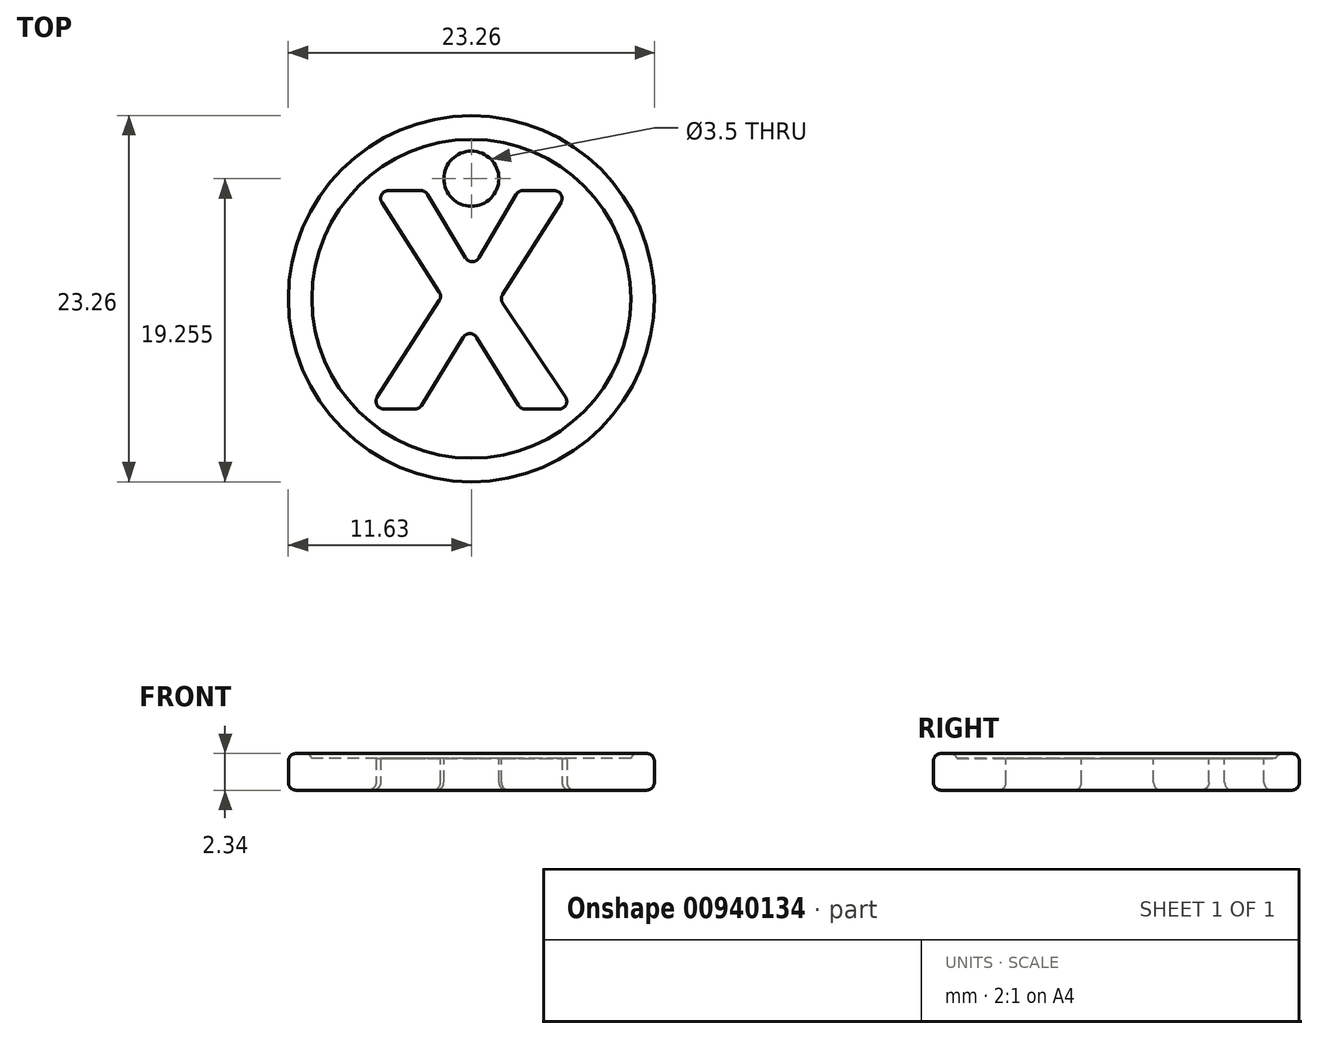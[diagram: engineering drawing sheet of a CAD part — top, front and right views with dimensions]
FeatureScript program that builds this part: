
annotation { "Feature Type Name" : "Feature", "Feature Type Description" : "" }
export const myFeature = defineFeature(function(context is Context, id is Id, definition is map)
    precondition{}
    {
        {
            var Q0;
            Q0=qCreatedBy(makeId("Front.planeOp"),FACE);
            var sketch = newSketch(context, id + "F0", { "sketchPlane" : qUnion([Q0])});
            skLineSegment(sketch, "E0", {"start": v(0, 0.86) * mm, "end": v(10.12, 0.86) * mm});
            skLineSegment(sketch, "E1", {"start": v(10.13, 0.86) * mm, "end": v(10.13, 1.17) * mm});
            skLineSegment(sketch, "E2", {"start": v(10.13, 1.16) * mm, "end": v(11.63, 1.16) * mm});
            skLineSegment(sketch, "E3", {"start": v(11.63, 1.17) * mm, "end": v(11.63, -1.17) * mm});
            skLineSegment(sketch, "E4", {"start": v(11.63, -1.17) * mm, "end": v(10.13, -1.17) * mm});
            skLineSegment(sketch, "E5", {"start": v(10.13, -1.17) * mm, "end": v(10.13, -1.16) * mm});
            skLineSegment(sketch, "E6", {"start": v(10.12, -1.17) * mm, "end": v(0, -1.17) * mm});
            skLineSegment(sketch, "E7", {"start": v(0, -1.17) * mm, "end": v(0, 0.86) * mm});
            skLineSegment(sketch, "E8", {"start": v(0, 10.48) * mm, "end": v(0, -13.78) * mm, "construction": true});
            skSolve(sketch);
        }
        {
            var Q0;
            Q0=makeQuery(id+"F0.imprint","IMPRINT",FACE,{"disambiguationData":[TD([[makeQuery(id+"F0.imprint","IMPRINT",EDGE,{"derivedFrom":sQuery(id+"F0.wireOp",EDGE,"E0")}),-1.0]])]});
            var Q1;
            Q1=sQuery(id+"F0.wireOp",EDGE,"E8");
            revolve(context, id + "F1", {"surfaceOperationType" : NewSurfaceOperationType.NEW, "entities" : qUnion([Q0]), "axis" : qUnion([Q1]), "revolveType" : RevolveType.FULL});
        }
        {
            var Q0;
            Q0=makeQuery(id+"F1.opRevolve","SWEPT_FACE",FACE,{"disambiguationData":[OSD([sQuery(id+"F0.wireOp",EDGE,"E0")])]});
            var sketch = newSketch(context, id + "F2", { "sketchPlane" : qUnion([Q0])});
            skText(sketch, "E9", { "text": "X", "fontName": "NotoSans-Bold.ttf"});
            const initialGuessF2  = {"E9": [-0.00647, -0.00701, 1, 0, 0.014]};
            skSetInitialGuess(sketch, initialGuessF2);
            skSolve(sketch);
        }
        {
            var Q0;
            Q0 = qSketchRegion(id + "F2", true);
            extrude(context, id + "F3", {"entities" : qUnion([Q0]), "operationType" : NewBodyOperationType.REMOVE, "oppositeDirection" : true, "depth" : 25 * mm, "offsetDistance" : 25 * mm});
        }
        {
            var Q0;
            Q0=makeQuery(id+"F1.opRevolve","SWEPT_FACE",FACE,{"disambiguationData":[OSD([sQuery(id+"F0.wireOp",EDGE,"E0")])]});
            var sketch = newSketch(context, id + "F4", { "sketchPlane" : qUnion([Q0])});
            skPoint(sketch, "E10", {"position": v(0, 7.63) * mm});
            skSolve(sketch);
        }
        {
            var Q0;
            Q0=sQuery(id+"F4.wireOp",VERTEX,"E10");
            var Q1;
            Q1=makeQuery(id+"F1.opRevolve","SWEPT_BODY",BODY,{"disambiguationData":[OSD([sQuery(id+"F0.wireOp",EDGE,"E0"),sQuery(id+"F0.wireOp",EDGE,"E1"),sQuery(id+"F0.wireOp",EDGE,"E2"),sQuery(id+"F0.wireOp",EDGE,"E3"),sQuery(id+"F0.wireOp",EDGE,"E4"),sQuery(id+"F0.wireOp",EDGE,"E5"),sQuery(id+"F0.wireOp",EDGE,"E6"),sQuery(id+"F0.wireOp",EDGE,"E7")])]});
            hole(context, id + "F5", {"style" : HoleStyle.SIMPLE, "endStyle" : HoleEndStyle.THROUGH, "holeDiameter" : 3.5 * mm, "majorDiameter" : 5 * mm, "isTappedThrough" : true, "tappedDepth" : 12 * mm, "tapClearance" : 3, "locations" : qUnion([Q0]), "scope" : qUnion([Q1])});
        }
        {
            var Q0;
            Q0=makeQuery(id+"F1.opRevolve","SWEPT_EDGE",EDGE,{"disambiguationData":[OSD([sQuery(id+"F0.wireOp",EDGE,"E2"),sQuery(id+"F0.wireOp",EDGE,"E3")])]});
            var Q1;
            Q1=makeQuery(id+"F1.opRevolve","SWEPT_EDGE",EDGE,{"disambiguationData":[OSD([sQuery(id+"F0.wireOp",EDGE,"E1"),sQuery(id+"F0.wireOp",EDGE,"E2")])]});
            var Q2;
            Q2=makeQuery(id+"F1.opRevolve","SWEPT_FACE",FACE,{"disambiguationData":[OSD([sQuery(id+"F0.wireOp",EDGE,"E3")])]});
            fillet(context, id + "F6", {"entities" : qUnion([Q0, Q1, Q2]), "radius" : 0.5 * mm, "tangentPropagation" : true, "allowEdgeOverflow" : false});
        }
        {
            var Q0;
            Q0=makeQuery(id+"F3.boolean.opBoolean","COPY",EDGE,{"derivedFrom":makeQuery(id+"F3.opExtrude","CAP_EDGE",EDGE,{"disambiguationData":[OSD([sQuery(id+"F2.wireOp",EDGE,"E9.sketch_text.stroke-5")])],"isStart":true})});
            var Q1;
            Q1=makeQuery(id+"F3.boolean.opBoolean","COPY",EDGE,{"derivedFrom":makeQuery(id+"F3.opExtrude","CAP_EDGE",EDGE,{"disambiguationData":[OSD([sQuery(id+"F2.wireOp",EDGE,"E9.sketch_text.stroke-11")])],"isStart":true})});
            var Q2;
            Q2=makeQuery(id+"F3.boolean.opBoolean","COPY",EDGE,{"derivedFrom":makeQuery(id+"F3.opExtrude","CAP_EDGE",EDGE,{"disambiguationData":[OSD([sQuery(id+"F2.wireOp",EDGE,"E9.sketch_text.stroke-10")])],"isStart":true})});
            var Q3;
            Q3=makeQuery(id+"F3.boolean.opBoolean","COPY",EDGE,{"derivedFrom":makeQuery(id+"F3.opExtrude","CAP_EDGE",EDGE,{"disambiguationData":[OSD([sQuery(id+"F2.wireOp",EDGE,"E9.sketch_text.stroke-6")])],"isStart":true})});
            var Q4;
            Q4=makeQuery(id+"F3.boolean.opBoolean","COPY",EDGE,{"derivedFrom":makeQuery(id+"F3.opExtrude","CAP_EDGE",EDGE,{"disambiguationData":[OSD([sQuery(id+"F2.wireOp",EDGE,"E9.sketch_text.stroke-9")])],"isStart":true})});
            var Q5;
            Q5=makeQuery(id+"F3.boolean.opBoolean","COPY",EDGE,{"derivedFrom":makeQuery(id+"F3.opExtrude","CAP_EDGE",EDGE,{"disambiguationData":[OSD([sQuery(id+"F2.wireOp",EDGE,"E9.sketch_text.stroke-3")])],"isStart":true})});
            var Q6;
            Q6=makeQuery(id+"F3.boolean.opBoolean","COPY",EDGE,{"derivedFrom":makeQuery(id+"F3.opExtrude","CAP_EDGE",EDGE,{"disambiguationData":[OSD([sQuery(id+"F2.wireOp",EDGE,"E9.sketch_text.stroke-2")])],"isStart":true})});
            var Q7;
            Q7=makeQuery(id+"F3.boolean.opBoolean","COPY",EDGE,{"derivedFrom":makeQuery(id+"F3.opExtrude","CAP_EDGE",EDGE,{"disambiguationData":[OSD([sQuery(id+"F2.wireOp",EDGE,"E9.sketch_text.stroke-8")])],"isStart":true})});
            var Q8;
            Q8=makeQuery(id+"F3.boolean.opBoolean","COPY",EDGE,{"derivedFrom":makeQuery(id+"F3.opExtrude","CAP_EDGE",EDGE,{"disambiguationData":[OSD([sQuery(id+"F2.wireOp",EDGE,"E9.sketch_text.stroke-0")])],"isStart":true})});
            var Q9;
            Q9=makeQuery(id+"F3.boolean.opBoolean","COPY",EDGE,{"derivedFrom":makeQuery(id+"F3.opExtrude","CAP_EDGE",EDGE,{"disambiguationData":[OSD([sQuery(id+"F2.wireOp",EDGE,"E9.sketch_text.stroke-4")])],"isStart":true})});
            var Q10;
            Q10=makeQuery(id+"F3.boolean.opBoolean","COPY",EDGE,{"derivedFrom":makeQuery(id+"F3.opExtrude","CAP_EDGE",EDGE,{"disambiguationData":[OSD([sQuery(id+"F2.wireOp",EDGE,"E9.sketch_text.stroke-1")])],"isStart":true})});
            var Q11;
            Q11=makeQuery(id+"F3.boolean.opBoolean","COPY",EDGE,{"derivedFrom":makeQuery(id+"F3.opExtrude","CAP_EDGE",EDGE,{"disambiguationData":[OSD([sQuery(id+"F2.wireOp",EDGE,"E9.sketch_text.stroke-7")])],"isStart":true})});
            var Q12;
            Q12=makeQuery(id+"F3.boolean.opBoolean","COPY",EDGE,{"derivedFrom":makeQuery(id+"F3.opExtrude","SWEPT_EDGE",EDGE,{"disambiguationData":[OSD([sQuery(id+"F2.wireOp",EDGE,"E9.sketch_text.stroke-3"),sQuery(id+"F2.wireOp",EDGE,"E9.sketch_text.stroke-4")])]})});
            var Q13;
            Q13=makeQuery(id+"F3.boolean.opBoolean","COPY",EDGE,{"derivedFrom":makeQuery(id+"F3.opExtrude","SWEPT_EDGE",EDGE,{"disambiguationData":[OSD([sQuery(id+"F2.wireOp",EDGE,"E9.sketch_text.stroke-0"),sQuery(id+"F2.wireOp",EDGE,"E9.sketch_text.stroke-11")])]})});
            var Q14;
            Q14=makeQuery(id+"F3.boolean.opBoolean","COPY",EDGE,{"derivedFrom":makeQuery(id+"F3.opExtrude","SWEPT_EDGE",EDGE,{"disambiguationData":[OSD([sQuery(id+"F2.wireOp",EDGE,"E9.sketch_text.stroke-2"),sQuery(id+"F2.wireOp",EDGE,"E9.sketch_text.stroke-3")])]})});
            var Q15;
            Q15=makeQuery(id+"F3.boolean.opBoolean","COPY",EDGE,{"derivedFrom":makeQuery(id+"F3.opExtrude","SWEPT_EDGE",EDGE,{"disambiguationData":[OSD([sQuery(id+"F2.wireOp",EDGE,"E9.sketch_text.stroke-10"),sQuery(id+"F2.wireOp",EDGE,"E9.sketch_text.stroke-11")])]})});
            var Q16;
            Q16=makeQuery(id+"F3.boolean.opBoolean","COPY",EDGE,{"derivedFrom":makeQuery(id+"F3.opExtrude","SWEPT_EDGE",EDGE,{"disambiguationData":[OSD([sQuery(id+"F2.wireOp",EDGE,"E9.sketch_text.stroke-7"),sQuery(id+"F2.wireOp",EDGE,"E9.sketch_text.stroke-8")])]})});
            var Q17;
            Q17=makeQuery(id+"F3.boolean.opBoolean","COPY",EDGE,{"derivedFrom":makeQuery(id+"F3.opExtrude","SWEPT_EDGE",EDGE,{"disambiguationData":[OSD([sQuery(id+"F2.wireOp",EDGE,"E9.sketch_text.stroke-4"),sQuery(id+"F2.wireOp",EDGE,"E9.sketch_text.stroke-5")])]})});
            var Q18;
            Q18=makeQuery(id+"F3.boolean.opBoolean","COPY",EDGE,{"derivedFrom":makeQuery(id+"F3.opExtrude","SWEPT_EDGE",EDGE,{"disambiguationData":[OSD([sQuery(id+"F2.wireOp",EDGE,"E9.sketch_text.stroke-5"),sQuery(id+"F2.wireOp",EDGE,"E9.sketch_text.stroke-6")])]})});
            var Q19;
            Q19=makeQuery(id+"F3.boolean.opBoolean","COPY",EDGE,{"derivedFrom":makeQuery(id+"F3.opExtrude","SWEPT_EDGE",EDGE,{"disambiguationData":[OSD([sQuery(id+"F2.wireOp",EDGE,"E9.sketch_text.stroke-9"),sQuery(id+"F2.wireOp",EDGE,"E9.sketch_text.stroke-10")])]})});
            var Q20;
            Q20=makeQuery(id+"F3.boolean.opBoolean","COPY",EDGE,{"derivedFrom":makeQuery(id+"F3.opExtrude","SWEPT_EDGE",EDGE,{"disambiguationData":[OSD([sQuery(id+"F2.wireOp",EDGE,"E9.sketch_text.stroke-8"),sQuery(id+"F2.wireOp",EDGE,"E9.sketch_text.stroke-9")])]})});
            var Q21;
            Q21=makeQuery(id+"F3.boolean.opBoolean","COPY",EDGE,{"derivedFrom":makeQuery(id+"F3.opExtrude","SWEPT_EDGE",EDGE,{"disambiguationData":[OSD([sQuery(id+"F2.wireOp",EDGE,"E9.sketch_text.stroke-0"),sQuery(id+"F2.wireOp",EDGE,"E9.sketch_text.stroke-1")])]})});
            var Q22;
            Q22=makeQuery(id+"F3.boolean.opBoolean","COPY",EDGE,{"derivedFrom":makeQuery(id+"F3.opExtrude","SWEPT_EDGE",EDGE,{"disambiguationData":[OSD([sQuery(id+"F2.wireOp",EDGE,"E9.sketch_text.stroke-1"),sQuery(id+"F2.wireOp",EDGE,"E9.sketch_text.stroke-2")])]})});
            var Q23;
            Q23=makeQuery(id+"F3.boolean.opBoolean","COPY",EDGE,{"derivedFrom":makeQuery(id+"F3.opExtrude","SWEPT_EDGE",EDGE,{"disambiguationData":[OSD([sQuery(id+"F2.wireOp",EDGE,"E9.sketch_text.stroke-6"),sQuery(id+"F2.wireOp",EDGE,"E9.sketch_text.stroke-7")])]})});
            var Q24;
            Q24=makeQuery(id+"F5.hole-0.boolean.opBoolean","COPY",EDGE,{"derivedFrom":makeQuery(id+"F5.hole-0.opRevolve","SWEPT_EDGE",EDGE,{"disambiguationData":[OSD([sQuery(id+"F5.hole-0.sketch.wireOp",EDGE,"core_line_2"),sQuery(id+"F5.hole-0.sketch.wireOp",EDGE,"core_line_3")])]})});
            fillet(context, id + "F7", {"entities" : qUnion([Q0, Q1, Q2, Q3, Q4, Q5, Q6, Q7, Q8, Q9, Q10, Q11, Q12, Q13, Q14, Q15, Q16, Q17, Q18, Q19, Q20, Q21, Q22, Q23, Q24]), "radius" : 0.5 * mm, "tangentPropagation" : true, "allowEdgeOverflow" : false});
        }
        {
            var Q0;
            Q0=makeQuery(id+"F1.opRevolve","SWEPT_FACE",FACE,{"disambiguationData":[OSD([sQuery(id+"F0.wireOp",EDGE,"E4"),sQuery(id+"F0.wireOp",EDGE,"E6")])]});
            fillet(context, id + "F8", {"entities" : qUnion([Q0]), "radius" : 0.5 * mm, "tangentPropagation" : true, "allowEdgeOverflow" : false});
        }
    });
